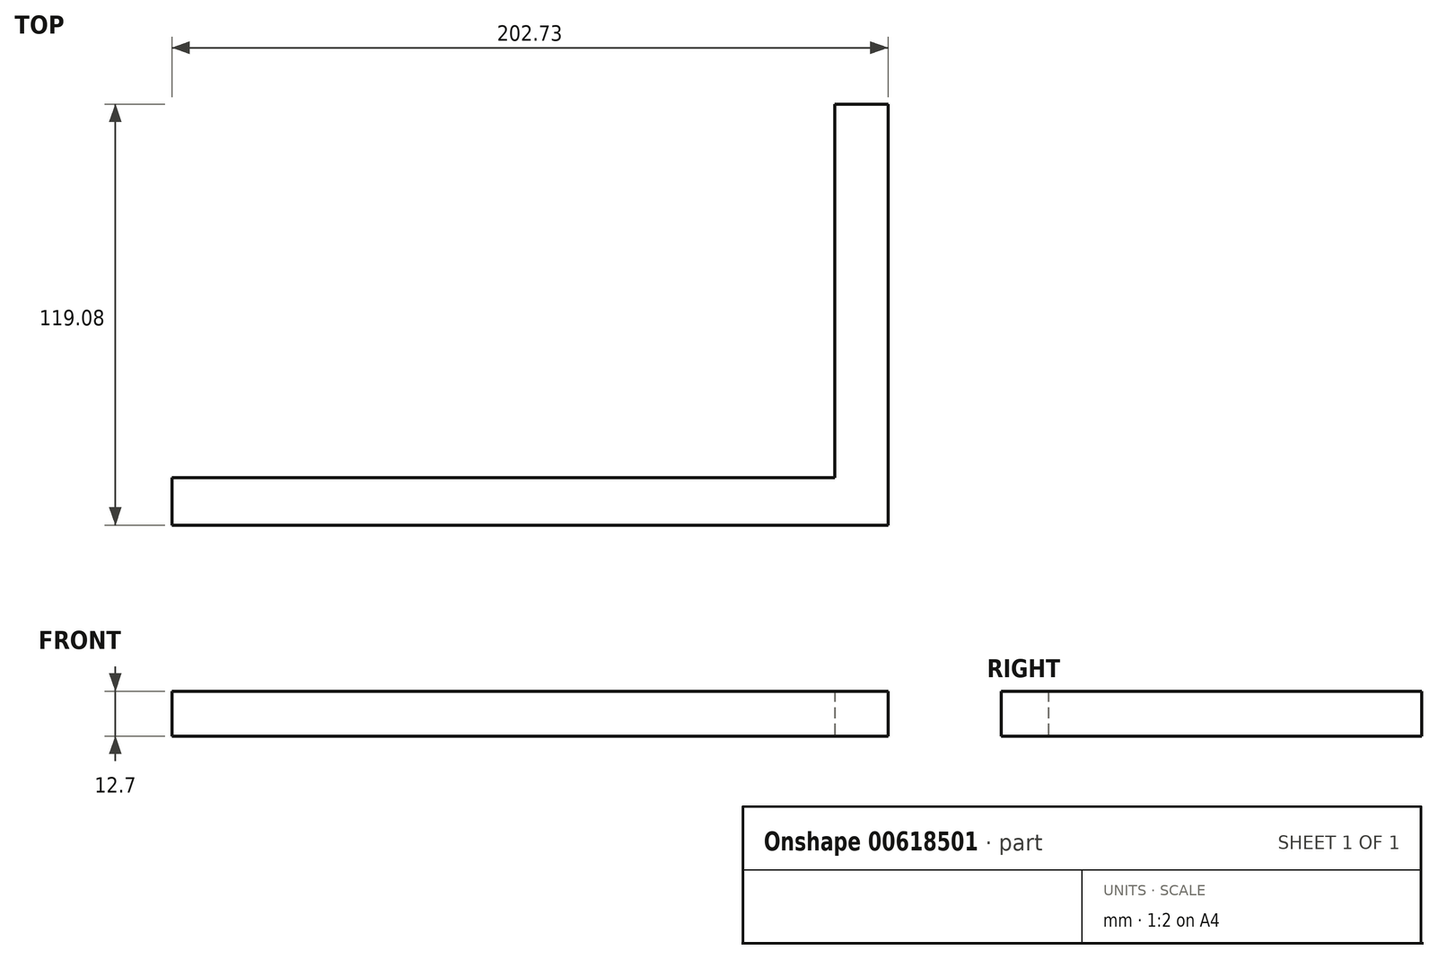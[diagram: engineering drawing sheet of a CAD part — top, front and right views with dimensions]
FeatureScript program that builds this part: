
annotation { "Feature Type Name" : "Feature", "Feature Type Description" : "" }
export const myFeature = defineFeature(function(context is Context, id is Id, definition is map)
    precondition{}
    {
        {
            var Q0;
            Q0=qCreatedBy(makeId("Top.planeOp"),FACE);
            var sketch = newSketch(context, id + "F0", { "sketchPlane" : qUnion([Q0])});
            skLineSegment(sketch, "E0.bottom", {"start": v(-104.28, -41.12) * mm, "end": v(83.32, -41.12) * mm});
            skLineSegment(sketch, "E0.top", {"start": v(-104.28, -54.5) * mm, "end": v(83.32, -54.5) * mm});
            skLineSegment(sketch, "E0.left", {"start": v(-104.28, -41.12) * mm, "end": v(-104.28, -54.5) * mm});
            skLineSegment(sketch, "E0.right", {"start": v(83.32, -41.12) * mm, "end": v(83.32, -54.5) * mm});
            skLineSegment(sketch, "E1.bottom", {"start": v(83.32, -54.5) * mm, "end": v(98.45, -54.5) * mm});
            skLineSegment(sketch, "E1.top", {"start": v(83.32, 64.59) * mm, "end": v(98.45, 64.59) * mm});
            skLineSegment(sketch, "E1.left", {"start": v(83.32, -54.5) * mm, "end": v(83.32, 64.59) * mm});
            skLineSegment(sketch, "E1.right", {"start": v(98.45, -54.5) * mm, "end": v(98.45, 64.59) * mm});
            skSolve(sketch);
        }
        {
            var Q0;
            {var subQ0=sQuery(id+"F0.wireOp",EDGE,"E0.bottom");Q0=makeQuery(id+"F0.imprint","IMPRINT",FACE,{"disambiguationData":[TD([[makeQuery(id+"F0.imprint","IMPRINT",EDGE,{"derivedFrom":subQ0}),-1.0]])]});}
            var Q1;
            {var subQ3=sQuery(id+"F0.wireOp",EDGE,"E1.bottom");Q1=makeQuery(id+"F0.imprint","IMPRINT",FACE,{"disambiguationData":[TD([[makeQuery(id+"F0.imprint","IMPRINT",EDGE,{"derivedFrom":subQ3}),1.0]])]});}
            extrude(context, id + "F1", {"entities" : qUnion([Q0, Q1]), "depth" : 12.7 * mm, "offsetDistance" : 25.4 * mm});
        }
    });
